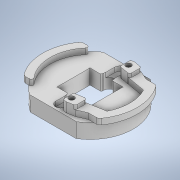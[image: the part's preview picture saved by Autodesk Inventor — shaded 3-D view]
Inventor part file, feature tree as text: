
AUTODESK INVENTOR PART (.ipt)
format: ipt  version: 2020 (Build 240168000, 168)  size: 499,200 bytes
history: native  units: mm
features: projected_geometry x15, sketch x12, extrude x10, fillet x5, other x3, revolve x1
ambient origin geometry x8: Origin, YZ Plane, XZ Plane, XY Plane, X Axis, Y Axis, Z Axis, Center Point
bodies: Body1 (feature_tree)
feature tree (46):
  other  "Твердое тело1"
  extrude  "Выдавливание1"  Depth=17.1mm
  extrude  "Выдавливание2"  Depth=17.1mm
  other  "РабПлоскость1"
  sketch  "Эскиз3"
  other  "РабОсь1"
  revolve  "Вращение1"
  extrude  "Выдавливание3"  Depth=25.0mm
  extrude  "Выдавливание4"  Depth=5.3mm
  extrude  "Выдавливание5"  Depth=44.7mm
  extrude  "Выдавливание6"  Depth=7.7mm TaperAngle=0.0deg
  extrude  "Выдавливание7"  Depth=5.0mm
  extrude  "Выдавливание8"  Depth=30.65mm
  sketch  "Эскиз10"
  extrude  "Выдавливание9"  Depth=2.5mm TaperAngle=0.0deg
  fillet  "Сопряжение1"  Radius=0.2mm
  fillet  "Сопряжение2"  [1 undecoded]
  fillet  "Сопряжение3"  Radius=1.85mm
  extrude  "Выдавливание10"  Depth=30.0mm
  fillet  "Сопряжение4"  Radius=2.0mm
  fillet  "Сопряжение5"  Radius=3.0mm
  sketch  "Эскиз1"
  sketch  "Эскиз2"
  projected_geometry  "Спроецированная петля1"
  projected_geometry  "Спроецированная петля2"
  sketch  "Эскиз4"
  projected_geometry  "Спроецированная петля3"
  sketch  "Эскиз5"
  sketch  "Эскиз6"
  projected_geometry  "Спроецированная петля4"
  sketch  "Эскиз7"
  projected_geometry  "Спроецированная петля5"
  sketch  "Эскиз8"
  projected_geometry  "Спроецированная петля6"
  projected_geometry  "Спроецированная петля7"
  projected_geometry  "Спроецированная петля8"
  sketch  "Эскиз9"
  projected_geometry  "Спроецированная петля9"
  projected_geometry  "Спроецированная петля10"
  projected_geometry  "Спроецированная петля11"
  projected_geometry  "Спроецированная петля12"
  sketch  "Эскиз11"
  sketch  "Эскиз12"
  projected_geometry  "Спроецированная петля13"
  projected_geometry  "Спроецированная петля14"
  projected_geometry  "Спроецированная петля15"
note: 1 required parameter value undecoded (feature->parameter linkage not recoverable at this tier; creation-order binding heuristic only, values carry confidence <= 0.55)
